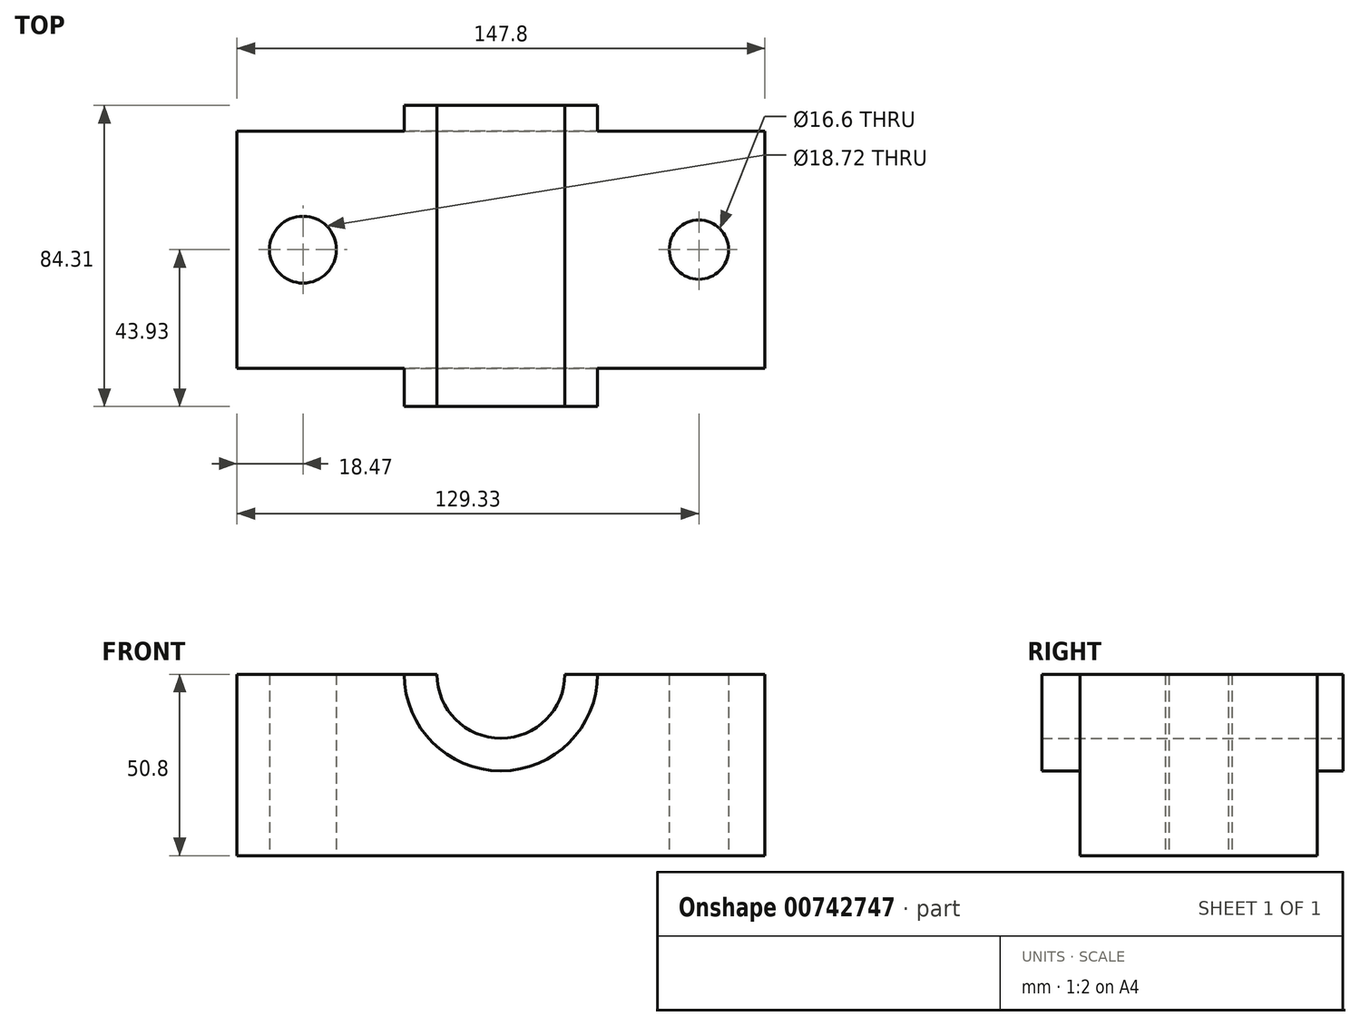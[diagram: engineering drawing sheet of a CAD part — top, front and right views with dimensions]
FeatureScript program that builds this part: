
annotation { "Feature Type Name" : "Feature", "Feature Type Description" : "" }
export const myFeature = defineFeature(function(context is Context, id is Id, definition is map)
    precondition{}
    {
        {
            var Q0;
            Q0=qCreatedBy(makeId("Top.planeOp"),FACE);
            var sketch = newSketch(context, id + "F0", { "sketchPlane" : qUnion([Q0])});
            skLineSegment(sketch, "E0.bottom", {"start": v(73.9, 33.19) * mm, "end": v(-73.9, 33.19) * mm});
            skLineSegment(sketch, "E0.top", {"start": v(73.9, -33.19) * mm, "end": v(-73.9, -33.19) * mm});
            skLineSegment(sketch, "E0.left", {"start": v(73.9, 33.19) * mm, "end": v(73.9, -33.19) * mm});
            skLineSegment(sketch, "E0.right", {"start": v(-73.9, 33.19) * mm, "end": v(-73.9, -33.19) * mm});
            skPoint(sketch, "E0.middle", {"position": v(0, 0) * mm});
            skLineSegment(sketch, "E1", {"start": v(0, 0) * mm, "end": v(-73.9, 0) * mm});
            skLineSegment(sketch, "E2", {"start": v(-73.9, 0) * mm, "end": v(-36.95, 0) * mm});
            skCircle(sketch, "E3", {"center": v(-55.43, 0) * mm, "radius": 9.36 * mm});
            skLineSegment(sketch, "E4", {"start": v(73.9, 0) * mm, "end": v(0, 0) * mm});
            skLineSegment(sketch, "E5", {"start": v(0, 0) * mm, "end": v(36.95, 0) * mm});
            skLineSegment(sketch, "E6", {"start": v(36.95, 0) * mm, "end": v(73.9, 0) * mm});
            skCircle(sketch, "E7", {"center": v(55.43, 0) * mm, "radius": 8.3 * mm});
            skSolve(sketch);
        }
        {
            var Q0;
            {var subQ14=sQuery(id+"F0.wireOp",EDGE,"E0.top");Q0=makeQuery(id+"F0.imprint","IMPRINT",FACE,{"disambiguationData":[TD([[makeQuery(id+"F0.imprint","IMPRINT",EDGE,{"derivedFrom":subQ14}),-1.0]])]});}
            var Q1;
            {var subQ8=sQuery(id+"F0.wireOp",EDGE,"E0.bottom");Q1=makeQuery(id+"F0.imprint","IMPRINT",FACE,{"disambiguationData":[TD([[makeQuery(id+"F0.imprint","IMPRINT",EDGE,{"derivedFrom":subQ8}),1.0]])]});}
            extrude(context, id + "F1", {"entities" : qUnion([Q0, Q1]), "depth" : 50.8 * mm, "offsetDistance" : 25.4 * mm});
        }
        {
            var Q0;
            Q0=makeQuery(id+"F1.opExtrude","SWEPT_FACE",FACE,{"disambiguationData":[OSD([sQuery(id+"F0.wireOp",EDGE,"E0.top")])]});
            var sketch = newSketch(context, id + "F2", { "sketchPlane" : qUnion([Q0])});
            skArc(sketch, "E8", {"start": v(-17.88, 50.8) * mm, "mid": v(0, 32.92) * mm, "end": v(17.88, 50.8) * mm});
            skArc(sketch, "E9", {"start": v(-27.09, 50.8) * mm, "mid": v(0, 23.71) * mm, "end": v(27.09, 50.8) * mm});
            skSolve(sketch);
        }
        {
            var Q0;
            {var subQ0=sQuery(id+"F2.wireOp",EDGE,"E8");Q0=makeQuery(id+"F2.imprint","IMPRINT",FACE,{"disambiguationData":[TD([[makeQuery(id+"F2.imprint","IMPRINT",EDGE,{"derivedFrom":subQ0}),-1.0]])]});}
            extrude(context, id + "F3", {"entities" : qUnion([Q0]), "operationType" : NewBodyOperationType.ADD, "oppositeDirection" : true, "depth" : 73.57 * mm, "offsetDistance" : 25.4 * mm});
        }
        {
            var Q0;
            {var subQ0=sQuery(id+"F2.wireOp",EDGE,"E8");var subQ1=sQuery(id+"F0.wireOp",EDGE,"E0.top");var subQ2=makeQuery(id+"F1.opExtrude","CAP_EDGE",EDGE,{"disambiguationData":[OSD([subQ1])],"isStart":false});Q0=makeQuery(id+"F3.boolean.opBoolean","MERGE",FACE,{"derivedFrom":[makeQuery(id+"F1.opExtrude","CAP_FACE",FACE,{"disambiguationData":[OSD([sQuery(id+"F0.wireOp",EDGE,"E0.bottom"),subQ1,sQuery(id+"F0.wireOp",EDGE,"E0.left"),sQuery(id+"F0.wireOp",EDGE,"E0.right"),sQuery(id+"F0.wireOp",EDGE,"E3"),sQuery(id+"F0.wireOp",EDGE,"E7")])],"isStart":false}),makeQuery(id+"F3.opExtrude","SWEPT_FACE",FACE,{"disambiguationData":[OSD([subQ1]),TDD([makeQuery(id+"F2.imprint","IMPRINT",EDGE,{"disambiguationData":[TD([[makeQuery(id+"F2.imprint","INTERSECT",VERTEX,{"disambiguationData":[OD(0.0)],"derivedFrom":[subQ2,subQ0]}),-1.0]])],"derivedFrom":subQ2})])]}),makeQuery(id+"F3.opExtrude","SWEPT_FACE",FACE,{"disambiguationData":[OSD([subQ1]),TDD([makeQuery(id+"F2.imprint","IMPRINT",EDGE,{"disambiguationData":[TD([[makeQuery(id+"F2.imprint","INTERSECT",VERTEX,{"disambiguationData":[OD(1.0)],"derivedFrom":[subQ2,subQ0]}),1.0]])],"derivedFrom":subQ2})])]})]});}
            var sketch = newSketch(context, id + "F4", { "sketchPlane" : qUnion([Q0])});
            skLineSegment(sketch, "E10", {"start": v(-17.88, 33.19) * mm, "end": v(-17.88, -33.19) * mm});
            skLineSegment(sketch, "E11", {"start": v(-17.88, -33.19) * mm, "end": v(-27.09, -33.19) * mm});
            skLineSegment(sketch, "E12", {"start": v(-27.09, -33.19) * mm, "end": v(-27.09, 33.19) * mm});
            skLineSegment(sketch, "E13", {"start": v(17.88, 33.19) * mm, "end": v(17.88, -33.19) * mm});
            skLineSegment(sketch, "E14", {"start": v(17.88, -33.19) * mm, "end": v(17.88, -22.5) * mm});
            skLineSegment(sketch, "E15", {"start": v(27.09, 33.19) * mm, "end": v(27.09, -33.19) * mm});
            skSolve(sketch);
        }
        {
            var Q0;
            Q0=makeQuery(id+"F1.opExtrude","SWEPT_FACE",FACE,{"disambiguationData":[OSD([sQuery(id+"F0.wireOp",EDGE,"E0.top")])]});
            var sketch = newSketch(context, id + "F5", { "sketchPlane" : qUnion([Q0])});
            skArc(sketch, "E16", {"start": v(-17.9, 50.8) * mm, "mid": v(0, 32.9) * mm, "end": v(17.9, 50.8) * mm});
            skArc(sketch, "E17", {"start": v(-27.05, 50.8) * mm, "mid": v(0, 23.75) * mm, "end": v(27.05, 50.8) * mm});
            skSolve(sketch);
        }
        {
            var Q0;
            {var subQ0=sQuery(id+"F5.wireOp",EDGE,"E16");Q0=makeQuery(id+"F5.imprint","IMPRINT",FACE,{"disambiguationData":[TD([[makeQuery(id+"F5.imprint","IMPRINT",EDGE,{"derivedFrom":subQ0}),-1.0]])]});}
            var sketch = newSketch(context, id + "F6", { "sketchPlane" : qUnion([Q0])});
            skSolve(sketch);
        }
        {
            var Q0;
            {var subQ0=sQuery(id+"F5.wireOp",EDGE,"E16");Q0=makeQuery(id+"F6.imprint","IMPRINT",FACE,{"disambiguationData":[TD([[makeQuery(id+"F6.imprint","IMPRINT",EDGE,{"derivedFrom":makeQuery(id+"F5.imprint","IMPRINT",EDGE,{"derivedFrom":subQ0})}),-1.0]])]});}
            extrude(context, id + "F7", {"entities" : qUnion([Q0]), "operationType" : NewBodyOperationType.ADD, "depth" : 10.74 * mm, "offsetDistance" : 25.4 * mm});
        }
        {
            var Q0;
            {var subQ6=sQuery(id+"F4.wireOp",EDGE,"E10");Q0=makeQuery(id+"F4.imprint","IMPRINT",FACE,{"disambiguationData":[TD([[makeQuery(id+"F4.imprint","IMPRINT",EDGE,{"derivedFrom":subQ6}),1.0]])]});}
            var sketch = newSketch(context, id + "F8", { "sketchPlane" : qUnion([Q0])});
            skSolve(sketch);
        }
        {
            var Q0;
            {var subQ0=sQuery(id+"F5.wireOp",EDGE,"E16");Q0=makeQuery(id+"F5.imprint","IMPRINT",FACE,{"disambiguationData":[TD([[makeQuery(id+"F5.imprint","IMPRINT",EDGE,{"derivedFrom":subQ0}),1.0]])]});}
            var Q1;
            {var subQ1=sQuery(id+"F0.wireOp",EDGE,"E0.bottom");var subQ2=sQuery(id+"F2.wireOp",EDGE,"E8");Q1=makeQuery(id+"F3.boolean.opBoolean","SPLIT",FACE,{"disambiguationData":[TD([makeQuery(id+"F3.opExtrude","SWEPT_FACE",FACE,{"disambiguationData":[OSD([subQ2])]})])],"derivedFrom":makeQuery(id+"F1.opExtrude","SWEPT_FACE",FACE,{"disambiguationData":[OSD([subQ1])]})});}
            extrude(context, id + "F9", {"entities" : qUnion([Q0, Q1]), "operationType" : NewBodyOperationType.REMOVE, "oppositeDirection" : true, "depth" : 197.7 * mm, "offsetDistance" : 25.4 * mm});
        }
    });
